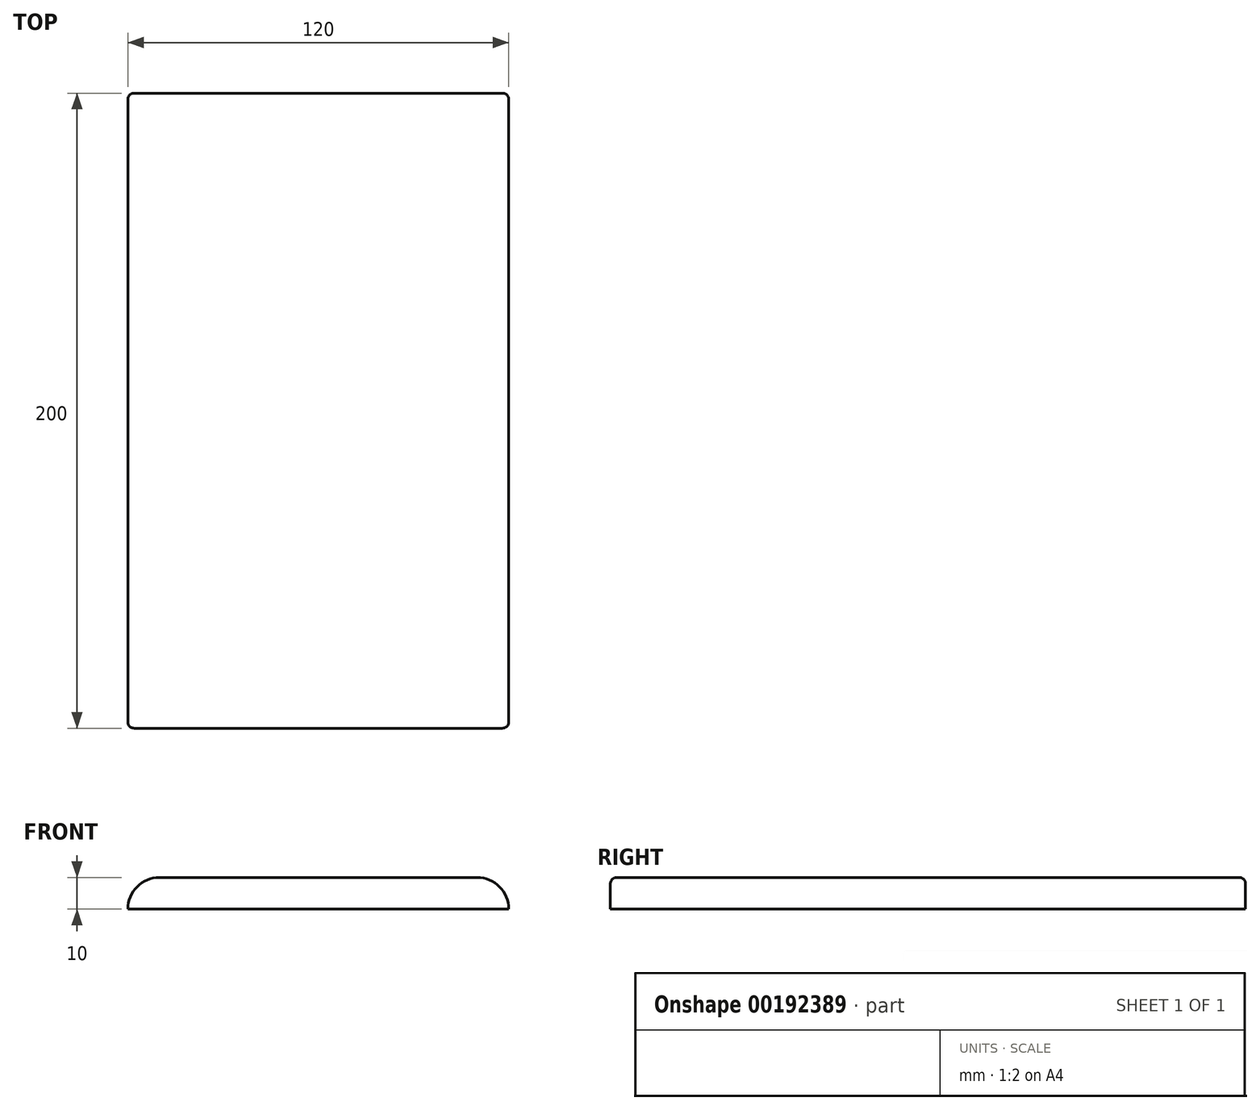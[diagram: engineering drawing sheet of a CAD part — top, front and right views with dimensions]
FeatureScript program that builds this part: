
annotation { "Feature Type Name" : "Feature", "Feature Type Description" : "" }
export const myFeature = defineFeature(function(context is Context, id is Id, definition is map)
    precondition{}
    {
        {
            var Q0;
            Q0=qCreatedBy(makeId("Front.planeOp"),FACE);
            var sketch = newSketch(context, id + "F0", { "sketchPlane" : qUnion([Q0])});
            skLineSegment(sketch, "E0", {"start": v(0, 0) * mm, "end": v(120, 0) * mm});
            skLineSegment(sketch, "E1", {"start": v(120, 0) * mm, "end": v(120, 0) * mm});
            skLineSegment(sketch, "E2", {"start": v(110, 10) * mm, "end": v(10, 10) * mm});
            skLineSegment(sketch, "E3", {"start": v(0, 0) * mm, "end": v(0, 0) * mm});
            skPoint(sketch, "E4.visualSharp", {"position": v(0, 10) * mm});
            skArc(sketch, "E4.filletArc", {"start": v(10, 10) * mm, "mid": v(2.93, 7.07) * mm, "end": v(0, 0) * mm});
            skPoint(sketch, "E5.visualSharp", {"position": v(120, 10) * mm});
            skArc(sketch, "E5.filletArc", {"start": v(120, 0) * mm, "mid": v(117.07, 7.07) * mm, "end": v(110, 10) * mm});
            skSolve(sketch);
        }
        {
            var Q0;
            Q0 = qSketchRegion(id + "F0", true);
            extrude(context, id + "F1", {"entities" : qUnion([Q0]), "depth" : 200 * mm});
        }
        {
            var Q0;
            Q0=makeQuery(id+"F1.opExtrude","CAP_EDGE",EDGE,{"disambiguationData":[OSD([sQuery(id+"F0.wireOp",EDGE,"E2")])],"isStart":false});
            fillet(context, id + "F2", {"entities" : qUnion([Q0]), "radius" : 2 * mm, "tangentPropagation" : true, "allowEdgeOverflow" : false});
        }
        {
            var Q0;
            Q0=makeQuery(id+"F1.opExtrude","CAP_EDGE",EDGE,{"disambiguationData":[OSD([sQuery(id+"F0.wireOp",EDGE,"E2")])],"isStart":true});
            fillet(context, id + "F3", {"entities" : qUnion([Q0]), "radius" : 2 * mm, "tangentPropagation" : true, "allowEdgeOverflow" : false});
        }
    });
